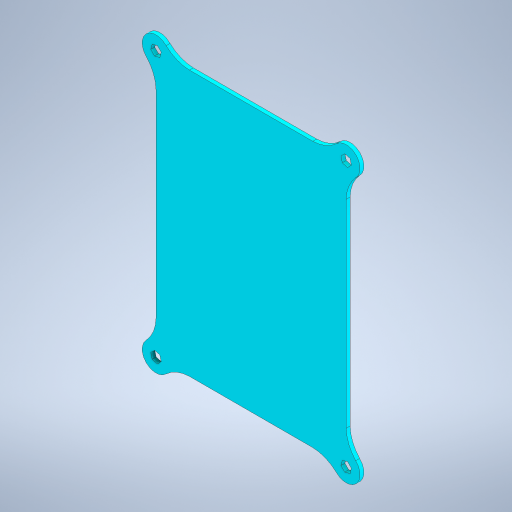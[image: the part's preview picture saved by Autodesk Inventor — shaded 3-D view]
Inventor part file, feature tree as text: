
AUTODESK INVENTOR PART (.ipt)
format: ipt  version: 2024 (Build 280153000, 153)  size: 304,128 bytes
history: native  units: mm
features: extrude x2, sketch x1
ambient origin geometry x8: Origin, YZ Plane, XZ Plane, XY Plane, X Axis, Y Axis, Z Axis, Center Point
bodies: Solid1 (feature_tree)
feature tree (3):
  sketch  "Sketch1"  dims[d0=87.0mm d1=107.0mm d2=145.0mm d4=5.0mm d5=5.0mm d6=2.0mm d7=0.0mm d8=5.0mm d9=0.0mm]
  extrude  "Extrusion1"  Depth=2.0mm TaperAngle=0.0deg
  extrude  "Extrusion2"  Depth=5.0mm TaperAngle=0.0deg
